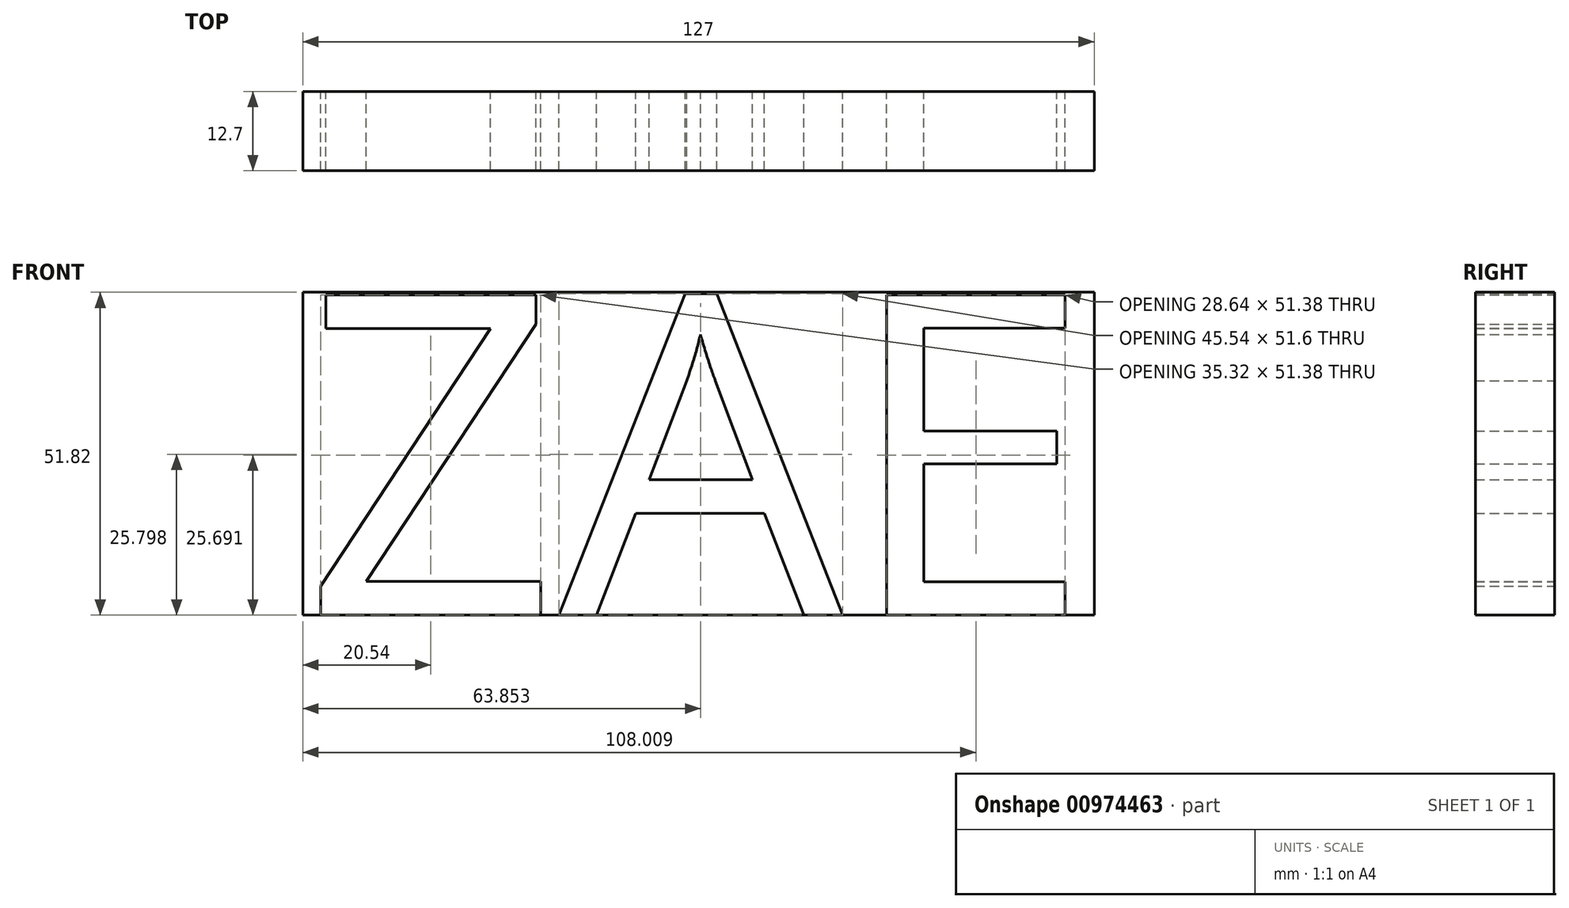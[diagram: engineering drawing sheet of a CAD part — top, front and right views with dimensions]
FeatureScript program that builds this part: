
annotation { "Feature Type Name" : "Feature", "Feature Type Description" : "" }
export const myFeature = defineFeature(function(context is Context, id is Id, definition is map)
    precondition{}
    {
        {
            var Q0;
            Q0=qCreatedBy(makeId("Front.planeOp"),FACE);
            var sketch = newSketch(context, id + "F0", { "sketchPlane" : qUnion([Q0])});
            skLineSegment(sketch, "E0.bottom", {"start": v(-25.4, -32.77) * mm, "end": v(101.6, -32.77) * mm});
            skLineSegment(sketch, "E0.top", {"start": v(-25.4, 19.05) * mm, "end": v(101.6, 19.05) * mm});
            skLineSegment(sketch, "E0.left", {"start": v(-25.4, -32.77) * mm, "end": v(-25.4, 19.05) * mm});
            skLineSegment(sketch, "E0.right", {"start": v(101.6, -32.77) * mm, "end": v(101.6, 19.05) * mm});
            skText(sketch, "E1", { "text": "ZAE", "fontName": "OpenSans-Regular.ttf"});
            const initialGuessF0  = {"E1": [-0.0254, -0.03277, 1, 0, 0.05182]};
            skSetInitialGuess(sketch, initialGuessF0);
            skSolve(sketch);
        }
        {
            var Q0;
            Q0=makeQuery(id+"F0.imprint","IMPRINT",FACE,{"disambiguationData":[TD([[makeQuery(id+"F0.imprint","IMPRINT",EDGE,{"derivedFrom":sQuery(id+"F0.wireOp",EDGE,"E0.bottom")}),1.0]])]});
            var Q1;
            {var subQ0=sQuery(id+"F0.wireOp",EDGE,"E1.sketch_text.stroke-10");Q1=makeQuery(id+"F0.imprint","IMPRINT",FACE,{"disambiguationData":[TD([[makeQuery(id+"F0.imprint","IMPRINT",EDGE,{"derivedFrom":subQ0}),1.0]])]});}
            var Q2;
            Q2=makeQuery(id+"F0.imprint","IMPRINT",FACE,{"disambiguationData":[TD([[makeQuery(id+"F0.imprint","IMPRINT",EDGE,{"derivedFrom":sQuery(id+"F0.wireOp",EDGE,"E1.sketch_text.stroke-18")}),1.0]])]});
            extrude(context, id + "F1", {"entities" : qUnion([Q0, Q1, Q2]), "depth" : 12.7 * mm, "offsetDistance" : 25.4 * mm});
        }
    });
